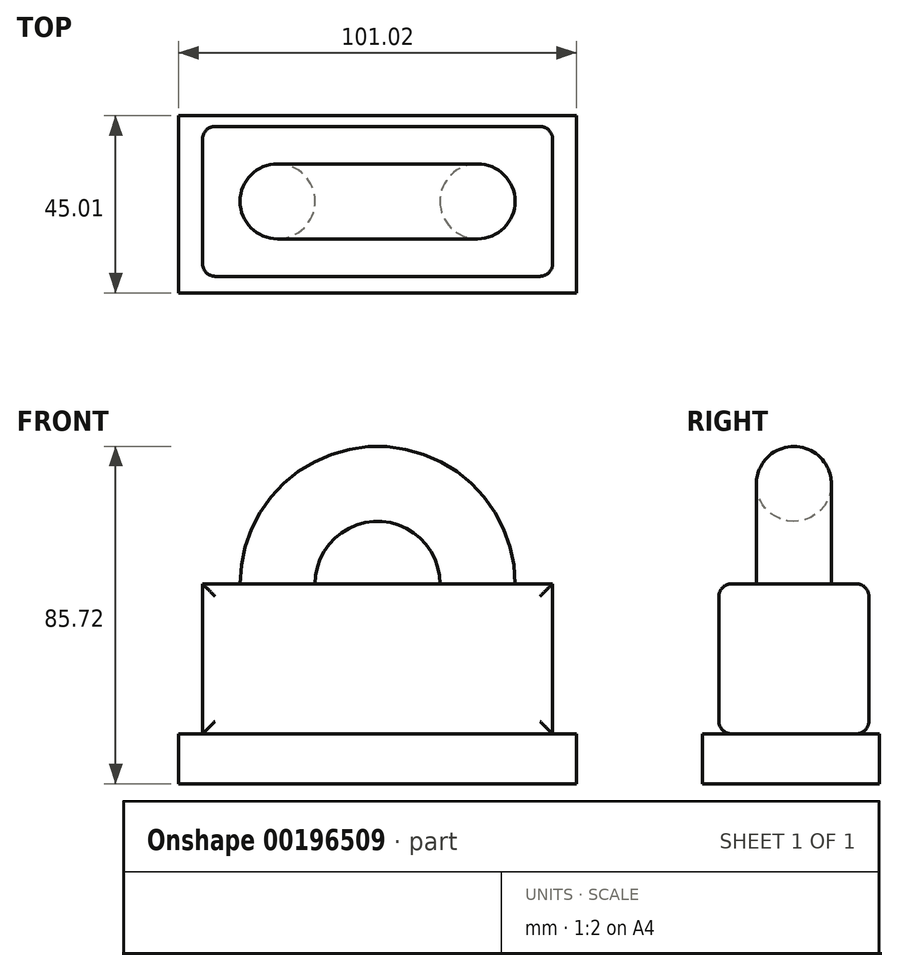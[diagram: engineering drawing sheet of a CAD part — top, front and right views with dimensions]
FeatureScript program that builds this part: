
annotation { "Feature Type Name" : "Feature", "Feature Type Description" : "" }
export const myFeature = defineFeature(function(context is Context, id is Id, definition is map)
    precondition{}
    {
        {
            var Q0;
            Q0=qCreatedBy(makeId("Front.planeOp"),FACE);
            var sketch = newSketch(context, id + "F0", { "sketchPlane" : qUnion([Q0])});
            skLineSegment(sketch, "E0.bottom", {"start": v(44.45, 19.05) * mm, "end": v(-44.45, 19.05) * mm});
            skLineSegment(sketch, "E0.top", {"start": v(44.45, -19.05) * mm, "end": v(-44.45, -19.05) * mm});
            skLineSegment(sketch, "E0.left", {"start": v(44.45, 19.05) * mm, "end": v(44.45, -19.05) * mm});
            skLineSegment(sketch, "E0.right", {"start": v(-44.45, 19.05) * mm, "end": v(-44.45, -19.05) * mm});
            skPoint(sketch, "E0.middle", {"position": v(0, 0) * mm});
            skSolve(sketch);
        }
        {
            var Q0;
            Q0=makeQuery(id+"F0.imprint","IMPRINT",FACE,{"disambiguationData":[TD([[makeQuery(id+"F0.imprint","IMPRINT",EDGE,{"derivedFrom":sQuery(id+"F0.wireOp",EDGE,"E0.bottom")}),1.0]])]});
            extrude(context, id + "F1", {"entities" : qUnion([Q0]), "depth" : 38.1 * mm});
        }
        {
            var Q0;
            Q0=makeQuery(id+"F1.opExtrude","SWEPT_FACE",FACE,{"disambiguationData":[OSD([sQuery(id+"F0.wireOp",EDGE,"E0.bottom")])]});
            var sketch = newSketch(context, id + "F2", { "sketchPlane" : qUnion([Q0])});
            skLineSegment(sketch, "E1", {"start": v(0, 0) * mm, "end": v(0, -49.48) * mm, "construction": true});
            skPoint(sketch, "E1.endSnap0", {"position": v(0, 0) * mm});
            skCircle(sketch, "E2", {"center": v(-25.4, -19.05) * mm, "radius": 9.53 * mm});
            skSolve(sketch);
        }
        {
            var Q0;
            Q0=makeQuery(id+"F2.imprint","IMPRINT",FACE,{"disambiguationData":[TD([[makeQuery(id+"F2.imprint","IMPRINT",EDGE,{"derivedFrom":sQuery(id+"F2.wireOp",EDGE,"E2")}),1.0]])]});
            var Q1;
            Q1=sQuery(id+"F2.wireOp",EDGE,"E1");
            revolve(context, id + "F3", {"operationType" : NewBodyOperationType.ADD, "entities" : qUnion([Q0]), "axis" : qUnion([Q1]), "revolveType" : RevolveType.FULL});
        }
        {
            var Q0;
            Q0=makeQuery(id+"F1.opExtrude","CAP_FACE",FACE,{"disambiguationData":[OSD([sQuery(id+"F0.wireOp",EDGE,"E0.bottom"),sQuery(id+"F0.wireOp",EDGE,"E0.top"),sQuery(id+"F0.wireOp",EDGE,"E0.left"),sQuery(id+"F0.wireOp",EDGE,"E0.right")])],"isStart":false});
            var Q1;
            Q1=makeQuery(id+"F1.opExtrude","CAP_FACE",FACE,{"disambiguationData":[OSD([sQuery(id+"F0.wireOp",EDGE,"E0.bottom"),sQuery(id+"F0.wireOp",EDGE,"E0.top"),sQuery(id+"F0.wireOp",EDGE,"E0.left"),sQuery(id+"F0.wireOp",EDGE,"E0.right")])],"isStart":true});
            fillet(context, id + "F4", {"entities" : qUnion([Q0, Q1]), "radius" : 3.17 * mm, "tangentPropagation" : true, "allowEdgeOverflow" : false});
        }
        {
            var Q0;
            Q0=makeQuery(id+"F1.opExtrude","SWEPT_FACE",FACE,{"disambiguationData":[OSD([sQuery(id+"F0.wireOp",EDGE,"E0.top")])]});
            var sketch = newSketch(context, id + "F5", { "sketchPlane" : qUnion([Q0])});
            skLineSegment(sketch, "E3.bottom", {"start": v(50.51, 42.31) * mm, "end": v(-50.51, 42.31) * mm});
            skLineSegment(sketch, "E3.top", {"start": v(50.51, -2.7) * mm, "end": v(-50.51, -2.7) * mm});
            skLineSegment(sketch, "E3.left", {"start": v(-50.51, -2.7) * mm, "end": v(-50.51, 42.31) * mm});
            skLineSegment(sketch, "E3.right", {"start": v(50.51, -2.7) * mm, "end": v(50.51, 42.31) * mm});
            skPoint(sketch, "E3.middle", {"position": v(0, 19.8) * mm});
            skSolve(sketch);
        }
        {
            var Q0;
            Q0 = qSketchRegion(id + "F5", true);
            extrude(context, id + "F6", {"entities" : qUnion([Q0]), "depth" : 12.7 * mm});
        }
    });
